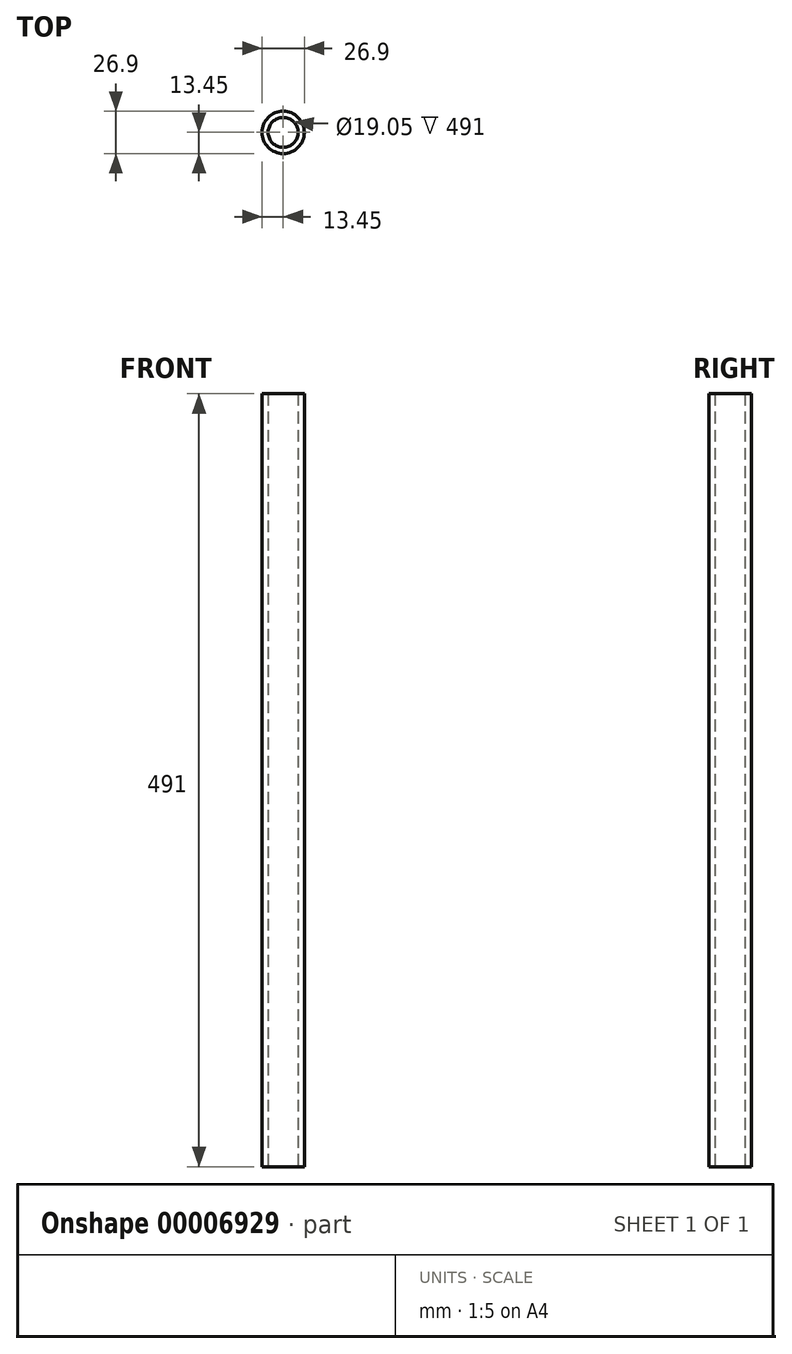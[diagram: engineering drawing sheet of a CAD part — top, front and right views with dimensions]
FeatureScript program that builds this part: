
annotation { "Feature Type Name" : "Feature", "Feature Type Description" : "" }
export const myFeature = defineFeature(function(context is Context, id is Id, definition is map)
    precondition{}
    {
        {
            var Q0;
            Q0=qCreatedBy(makeId("Top.planeOp"),FACE);
            var sketch = newSketch(context, id + "F0", { "sketchPlane" : qUnion([Q0])});
            skCircle(sketch, "E0", {"center": v(0, 0) * mm, "radius": 13.45 * mm});
            skCircle(sketch, "E1", {"center": v(0, 0) * mm, "radius": 9.53 * mm});
            skSolve(sketch);
        }
        {
            var Q0;
            Q0=makeQuery(id+"F0.imprint","IMPRINT",FACE,{"disambiguationData":[TD([[makeQuery(id+"F0.imprint","IMPRINT",EDGE,{"derivedFrom":sQuery(id+"F0.wireOp",EDGE,"E0")}),1.0]])]});
            extrude(context, id + "F1", {"entities" : qUnion([Q0]), "depth" : (491) * mm});
        }
    });
